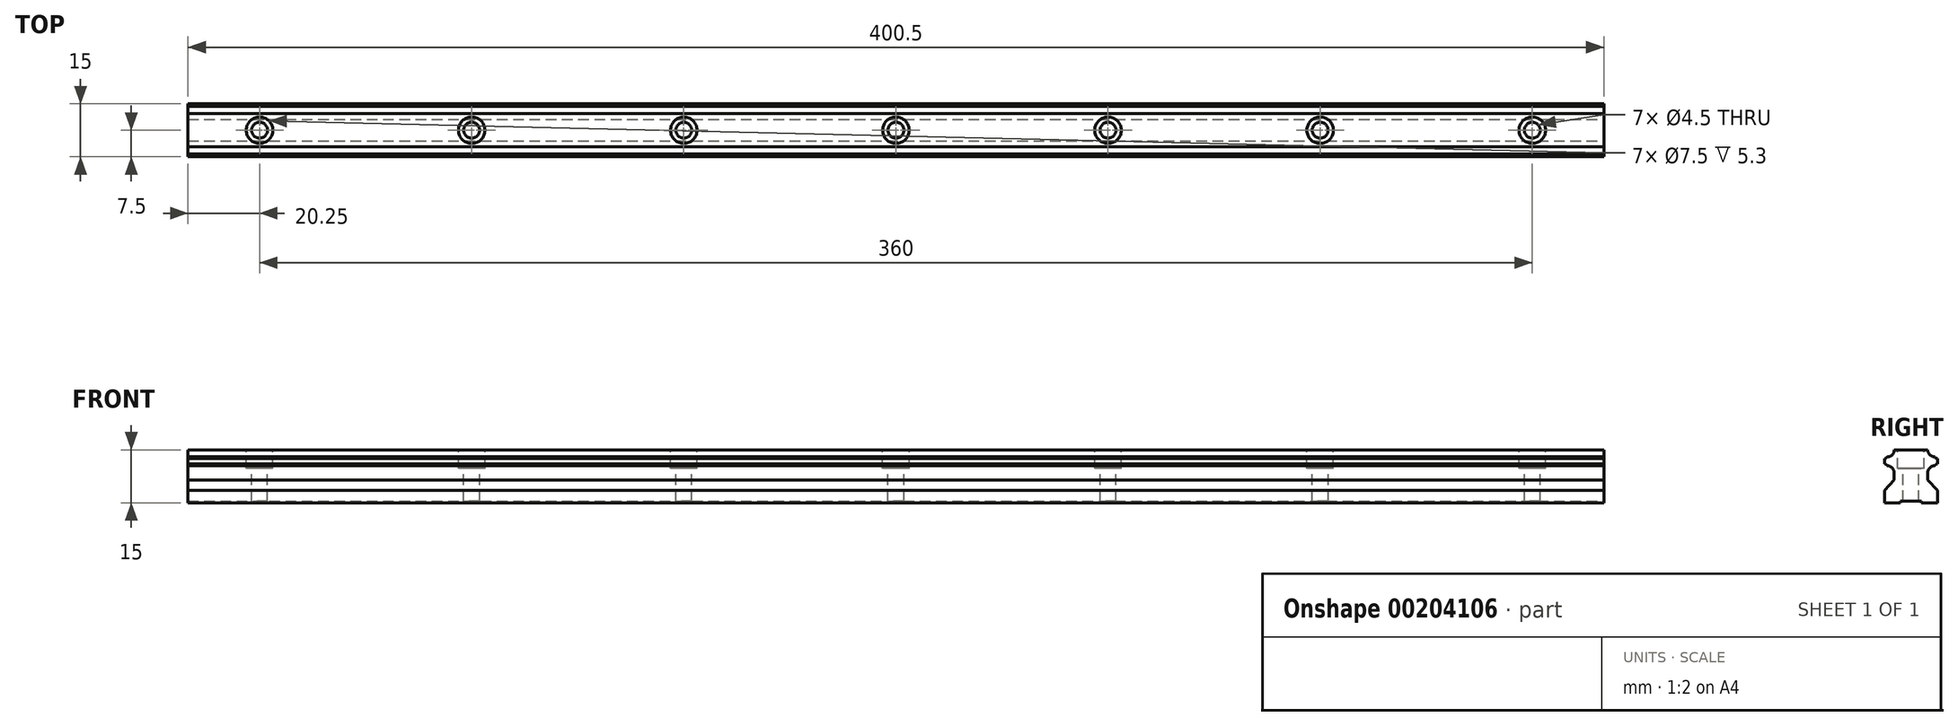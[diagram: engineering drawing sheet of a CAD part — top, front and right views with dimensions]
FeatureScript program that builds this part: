
annotation { "Feature Type Name" : "Feature", "Feature Type Description" : "" }
export const myFeature = defineFeature(function(context is Context, id is Id, definition is map)
    precondition{}
    {
        {
            var Q0;
            Q0=qCreatedBy(makeId("Right.planeOp"),FACE);
            var sketch = newSketch(context, id + "F0", { "sketchPlane" : qUnion([Q0])});
            skLineSegment(sketch, "E0", {"start": v(0, 23.93) * mm, "end": v(0, 0) * mm, "construction": true});
            skLineSegment(sketch, "E1", {"start": v(0, 0) * mm, "end": v(19.38, 0) * mm, "construction": true});
            skLineSegment(sketch, "E2", {"start": v(-7.5, -7.5) * mm, "end": v(7.5, -7.5) * mm});
            skLineSegment(sketch, "E3", {"start": v(7.5, -7.5) * mm, "end": v(7.5, 7.5) * mm});
            skLineSegment(sketch, "E4", {"start": v(7.5, 7.5) * mm, "end": v(-7.5, 7.5) * mm});
            skLineSegment(sketch, "E5", {"start": v(-7.5, 7.5) * mm, "end": v(-7.5, -7.5) * mm});
            skSolve(sketch);
        }
        {
            var Q0;
            Q0 = qSketchRegion(id + "F0", true);
            extrude(context, id + "F1", {"entities" : qUnion([Q0]), "endBound" : BoundingType.SYMMETRIC, "depth" : 400.5 * mm});
        }
        {
            var Q0;
            Q0=makeQuery(id+"F1.opExtrude","CAP_FACE",FACE,{"disambiguationData":[OSD([sQuery(id+"F0.wireOp",EDGE,"E2"),sQuery(id+"F0.wireOp",EDGE,"E3"),sQuery(id+"F0.wireOp",EDGE,"E4"),sQuery(id+"F0.wireOp",EDGE,"E5")])],"isStart":false});
            var sketch = newSketch(context, id + "F2", { "sketchPlane" : qUnion([Q0])});
            skLineSegment(sketch, "E6", {"start": v(0, 7.5) * mm, "end": v(0, -7.5) * mm, "construction": true});
            skLineSegment(sketch, "E7", {"start": v(0, 7.5) * mm, "end": v(-4.75, 7.5) * mm});
            skLineSegment(sketch, "E8", {"start": v(-7.5, 5) * mm, "end": v(-7.5, 3.5) * mm});
            skLineSegment(sketch, "E9", {"start": v(-4.75, 1) * mm, "end": v(-4.75, -1) * mm});
            skLineSegment(sketch, "E10", {"start": v(-4.75, -1) * mm, "end": v(-7.5, -4) * mm});
            skLineSegment(sketch, "E11", {"start": v(-7.5, -4) * mm, "end": v(-7.5, -7.5) * mm});
            skLineSegment(sketch, "E12", {"start": v(-7.5, -7.5) * mm, "end": v(-3, -7.5) * mm});
            skArc(sketch, "E13", {"start": v(-6.75, 5.5) * mm, "mid": v(-5.34, 6.09) * mm, "end": v(-4.75, 7.5) * mm});
            skLineSegment(sketch, "E14", {"start": v(-7.5, 4.25) * mm, "end": v(0, 4.25) * mm, "construction": true});
            skArc(sketch, "E15", {"start": v(-7.5, 5) * mm, "mid": v(-7.05, 5.14) * mm, "end": v(-6.75, 5.5) * mm});
            skArc(sketch, "E16.MirrorCS", {"start": v(-6.75, 3) * mm, "mid": v(-5.34, 2.41) * mm, "end": v(-4.75, 1) * mm});
            skArc(sketch, "E17.MirrorCS", {"start": v(-7.5, 3.5) * mm, "mid": v(-7.05, 3.36) * mm, "end": v(-6.75, 3) * mm});
            skLineSegment(sketch, "E18", {"start": v(-6.75, 5.5) * mm, "end": v(-6.75, 9.57) * mm, "construction": true});
            skLineSegment(sketch, "E19", {"start": v(0, -7) * mm, "end": v(-3, -7) * mm});
            skLineSegment(sketch, "E20", {"start": v(-3, -7) * mm, "end": v(-3, -7.5) * mm});
            skLineSegment(sketch, "E21", {"start": v(-3, -7.5) * mm, "end": v(0, -7.5) * mm, "construction": true});
            skLineSegment(sketch, "E22.MirrorCS", {"start": v(0, -7) * mm, "end": v(3, -7) * mm});
            skLineSegment(sketch, "E23.MirrorCS", {"start": v(3, -7) * mm, "end": v(3, -7.5) * mm});
            skLineSegment(sketch, "E24.MirrorCS", {"start": v(7.5, -7.5) * mm, "end": v(3, -7.5) * mm});
            skLineSegment(sketch, "E25.MirrorCS", {"start": v(7.5, -4) * mm, "end": v(7.5, -7.5) * mm});
            skLineSegment(sketch, "E26.MirrorCS", {"start": v(4.75, -1) * mm, "end": v(7.5, -4) * mm});
            skLineSegment(sketch, "E27.MirrorCS", {"start": v(4.75, 1) * mm, "end": v(4.75, -1) * mm});
            skArc(sketch, "E28.MirrorCS", {"start": v(6.75, 3) * mm, "mid": v(5.34, 2.41) * mm, "end": v(4.75, 1) * mm});
            skArc(sketch, "E29.MirrorCS", {"start": v(7.5, 3.5) * mm, "mid": v(7.05, 3.36) * mm, "end": v(6.75, 3) * mm});
            skLineSegment(sketch, "E30.MirrorCS", {"start": v(0, 7.5) * mm, "end": v(4.75, 7.5) * mm});
            skLineSegment(sketch, "E31.MirrorCS", {"start": v(7.5, 5) * mm, "end": v(7.5, 3.5) * mm});
            skArc(sketch, "E32.MirrorCS", {"start": v(7.5, 5) * mm, "mid": v(7.05, 5.14) * mm, "end": v(6.75, 5.5) * mm});
            skArc(sketch, "E33.MirrorCS", {"start": v(6.75, 5.5) * mm, "mid": v(5.34, 6.09) * mm, "end": v(4.75, 7.5) * mm});
            skLineSegment(sketch, "E34", {"start": v(-6.75, 5.5) * mm, "end": v(-9.84, 5.5) * mm, "construction": true});
            skSolve(sketch);
        }
        {
            var Q0;
            Q0 = qSketchRegion(id + "F2", true);
            extrude(context, id + "F3", {"entities" : qUnion([Q0]), "operationType" : NewBodyOperationType.INTERSECT, "endBound" : BoundingType.UP_TO_NEXT, "oppositeDirection" : true, "depth" : 25 * mm});
        }
        {
            var Q0;
            Q0=makeQuery(id+"F1.opExtrude","SWEPT_FACE",FACE,{"disambiguationData":[OSD([sQuery(id+"F0.wireOp",EDGE,"E4")])]});
            var sketch = newSketch(context, id + "F4", { "sketchPlane" : qUnion([Q0])});
            skLineSegment(sketch, "E35", {"start": v(-200.25, 0) * mm, "end": v(200.25, 0) * mm, "construction": true});
            skPoint(sketch, "E35.startSnap0", {"position": v(-200.25, 0) * mm});
            skPoint(sketch, "E36", {"position": v(0, 0) * mm});
            skPoint(sketch, "E37", {"position": v(60, 0) * mm});
            skPoint(sketch, "E38", {"position": v(120, 0) * mm});
            skPoint(sketch, "E39", {"position": v(180, 0) * mm});
            skLineSegment(sketch, "E40", {"start": v(0, 0) * mm, "end": v(0, 51.54) * mm, "construction": true});
            skPoint(sketch, "E41.MirrorP", {"position": v(-180, 0) * mm});
            skPoint(sketch, "E42.MirrorP", {"position": v(-60, 0) * mm});
            skPoint(sketch, "E43.MirrorP", {"position": v(-120, 0) * mm});
            skSolve(sketch);
        }
        {
            var Q0;
            Q0=sQuery(id+"F4.wireOp",VERTEX,"E41.MirrorP");
            var Q1;
            Q1=sQuery(id+"F4.wireOp",VERTEX,"E43.MirrorP");
            var Q2;
            Q2=sQuery(id+"F4.wireOp",VERTEX,"E42.MirrorP");
            var Q3;
            Q3=sQuery(id+"F4.wireOp",VERTEX,"E36");
            var Q4;
            Q4=sQuery(id+"F4.wireOp",VERTEX,"E37");
            var Q5;
            Q5=sQuery(id+"F4.wireOp",VERTEX,"E38");
            var Q6;
            Q6=sQuery(id+"F4.wireOp",VERTEX,"E39");
            var Q7;
            Q7=makeQuery(id+"F1.opExtrude","SWEPT_BODY",BODY,{"disambiguationData":[OSD([sQuery(id+"F0.wireOp",EDGE,"E2"),sQuery(id+"F0.wireOp",EDGE,"E3"),sQuery(id+"F0.wireOp",EDGE,"E4"),sQuery(id+"F0.wireOp",EDGE,"E5")])]});
            hole(context, id + "F5", {"style" : HoleStyle.C_BORE, "endStyle" : HoleEndStyle.THROUGH, "holeDiameter" : 4.5 * mm, "cBoreDiameter" : 7.5 * mm, "cBoreDepth" : 5.3 * mm, "locations" : qUnion([Q0, Q1, Q2, Q3, Q4, Q5, Q6]), "scope" : qUnion([Q7]), "isTappedThrough" : true});
        }
    });
